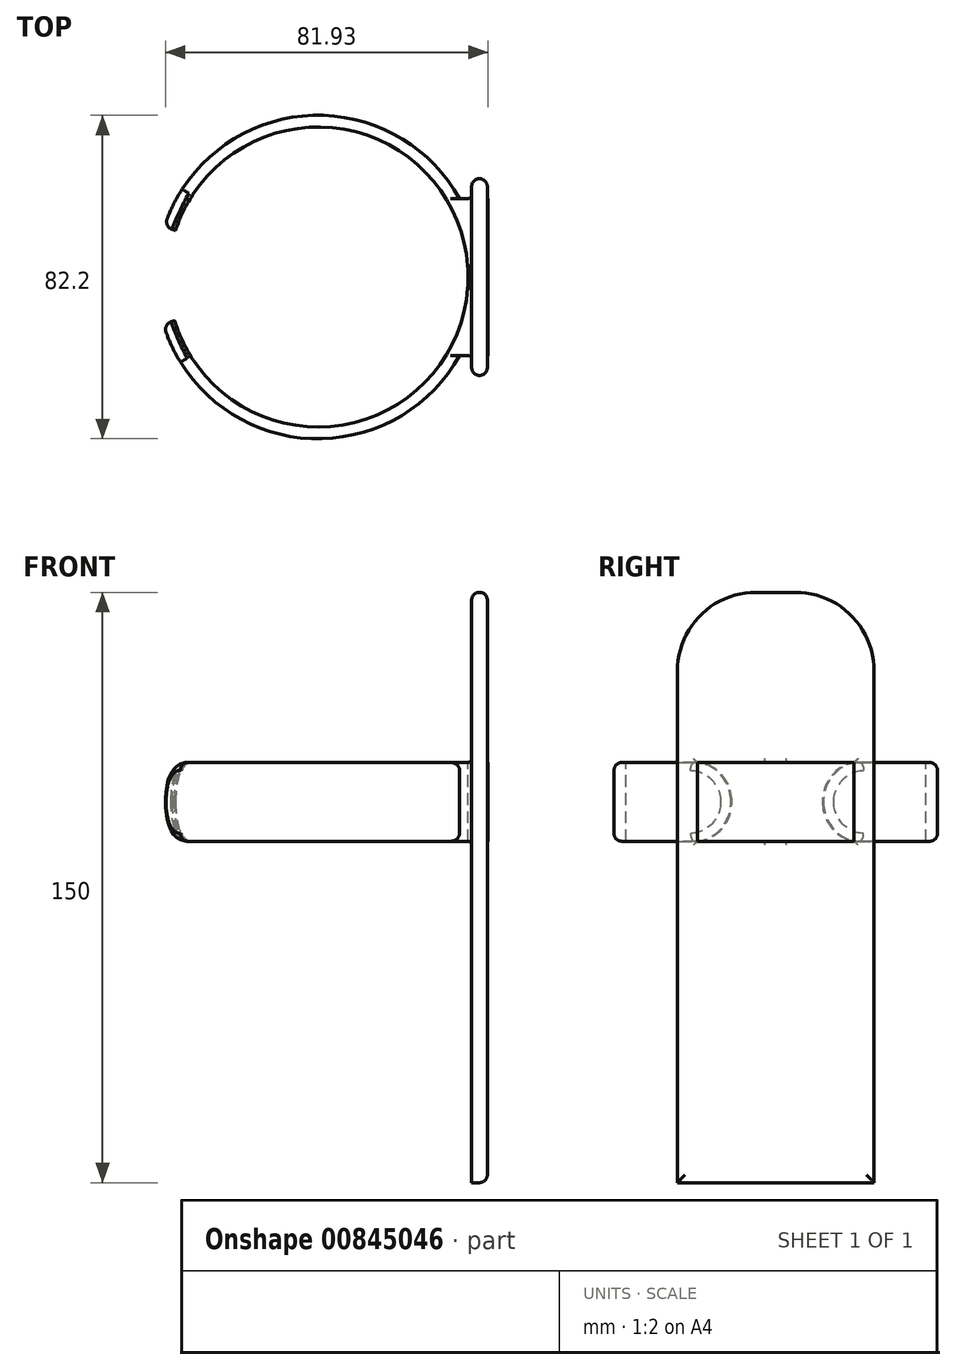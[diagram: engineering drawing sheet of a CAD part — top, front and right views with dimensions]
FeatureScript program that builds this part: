
annotation { "Feature Type Name" : "Feature", "Feature Type Description" : "" }
export const myFeature = defineFeature(function(context is Context, id is Id, definition is map)
    precondition{}
    {
        {
            var Q0;
            Q0=qCreatedBy(makeId("Top.planeOp"),FACE);
            var sketch = newSketch(context, id + "F0", { "sketchPlane" : qUnion([Q0])});
            skArc(sketch, "E0", {"start": v(-39.31, -11.99) * mm, "mid": v(41.1, -0.41) * mm, "end": v(-39.06, 12.77) * mm});
            skArc(sketch, "E1.0", {"start": v(-36.44, -11.11) * mm, "mid": v(38.1, -0.38) * mm, "end": v(-36.21, 11.84) * mm});
            skLineSegment(sketch, "E2", {"start": v(-39.06, 12.77) * mm, "end": v(-36.21, 11.84) * mm});
            skLineSegment(sketch, "E3", {"start": v(-36.44, -11.11) * mm, "end": v(-39.31, -11.99) * mm});
            skLineSegment(sketch, "E4", {"start": v(35.95, 19.92) * mm, "end": v(43.16, 19.92) * mm});
            skLineSegment(sketch, "E5", {"start": v(43.16, 19.92) * mm, "end": v(43.16, 0) * mm});
            skLineSegment(sketch, "E6.MirrorCS", {"start": v(43.16, -19.92) * mm, "end": v(43.16, 0) * mm});
            skLineSegment(sketch, "E7.MirrorCS", {"start": v(35.95, -19.92) * mm, "end": v(43.16, -19.92) * mm});
            skSolve(sketch);
        }
        {
            var Q0;
            Q0=makeQuery(id+"F0.imprint","IMPRINT",FACE,{"disambiguationData":[TD([[makeQuery(id+"F0.imprint","IMPRINT",EDGE,{"derivedFrom":sQuery(id+"F0.wireOp",EDGE,"E0")}),1.0]])]});
            var Q1;
            {var subQ0=sQuery(id+"F0.wireOp",EDGE,"E4");Q1=makeQuery(id+"F0.imprint","IMPRINT",FACE,{"disambiguationData":[TD([[makeQuery(id+"F0.imprint","IMPRINT",EDGE,{"derivedFrom":subQ0}),-1.0]])]});}
            extrude(context, id + "F1", {"entities" : qUnion([Q0, Q1]), "oppositeDirection" : true, "depth" : 20 * mm, "offsetDistance" : 25 * mm});
        }
        {
            var Q0;
            Q0=makeQuery(id+"F1.opExtrude","CAP_EDGE",EDGE,{"disambiguationData":[OSD([sQuery(id+"F0.wireOp",EDGE,"E2")])],"isStart":false});
            var Q1;
            Q1=makeQuery(id+"F1.opExtrude","CAP_EDGE",EDGE,{"disambiguationData":[OSD([sQuery(id+"F0.wireOp",EDGE,"E2")])],"isStart":true});
            var Q2;
            Q2=makeQuery(id+"F1.opExtrude","CAP_EDGE",EDGE,{"disambiguationData":[OSD([sQuery(id+"F0.wireOp",EDGE,"E3")])],"isStart":true});
            var Q3;
            Q3=makeQuery(id+"F1.opExtrude","CAP_EDGE",EDGE,{"disambiguationData":[OSD([sQuery(id+"F0.wireOp",EDGE,"E3")])],"isStart":false});
            fillet(context, id + "F2", {"entities" : qUnion([Q0, Q1, Q2, Q3]), "radius" : 10 * mm, "tangentPropagation" : true, "allowEdgeOverflow" : false});
        }
        {
            var Q0;
            Q0=makeQuery(id+"F1.opExtrude","CAP_EDGE",EDGE,{"disambiguationData":[OSD([sQuery(id+"F0.wireOp",EDGE,"E0")])],"isStart":true});
            fillet(context, id + "F3", {"entities" : qUnion([Q0]), "radius" : 2 * mm, "tangentPropagation" : true, "allowEdgeOverflow" : false});
        }
        {
            var Q0;
            Q0=qCreatedBy(makeId("Right.planeOp"),FACE);
            cPlane(context, id + "F4", {"entities" : qUnion([Q0]), "cplaneType" : CPlaneType.OFFSET, "offset" : 39 * mm, "width" : 150 * mm, "height" : 150 * mm});
        }
        {
            var Q0;
            Q0=qCreatedBy(id+"F4.planeOp",FACE);
            var sketch = newSketch(context, id + "F5", { "sketchPlane" : qUnion([Q0])});
            skLineSegment(sketch, "E8", {"start": v(0, 43.25) * mm, "end": v(25, 43.25) * mm});
            skLineSegment(sketch, "E9", {"start": v(25, 43.25) * mm, "end": v(25, -106.75) * mm});
            skLineSegment(sketch, "E10", {"start": v(25, -106.75) * mm, "end": v(0, -106.75) * mm});
            skLineSegment(sketch, "E11.MirrorCS", {"start": v(-25, -106.75) * mm, "end": v(0, -106.75) * mm});
            skLineSegment(sketch, "E12.MirrorCS", {"start": v(0, 43.25) * mm, "end": v(-25, 43.25) * mm});
            skLineSegment(sketch, "E13.MirrorCS", {"start": v(-25, 43.25) * mm, "end": v(-25, -106.75) * mm});
            skSolve(sketch);
        }
        {
            var Q0;
            Q0=makeQuery(id+"F5.imprint","IMPRINT",FACE,{"disambiguationData":[TD([[makeQuery(id+"F5.imprint","IMPRINT",EDGE,{"derivedFrom":sQuery(id+"F5.wireOp",EDGE,"E8")}),-1.0]])]});
            extrude(context, id + "F6", {"entities" : qUnion([Q0]), "operationType" : NewBodyOperationType.ADD, "depth" : 4 * mm, "offsetDistance" : 25 * mm});
        }
        {
            var Q0;
            Q0=makeQuery(id+"F6.opExtrude","SWEPT_EDGE",EDGE,{"disambiguationData":[OSD([sQuery(id+"F5.wireOp",EDGE,"E12.MirrorCS"),sQuery(id+"F5.wireOp",EDGE,"E13.MirrorCS")])]});
            var Q1;
            Q1=makeQuery(id+"F6.opExtrude","SWEPT_EDGE",EDGE,{"disambiguationData":[OSD([sQuery(id+"F5.wireOp",EDGE,"E8"),sQuery(id+"F5.wireOp",EDGE,"E9")])]});
            fillet(context, id + "F7", {"entities" : qUnion([Q0, Q1]), "radius" : 20 * mm, "tangentPropagation" : true, "allowEdgeOverflow" : false});
        }
        {
            var Q0;
            Q0=makeQuery(id+"F6.opExtrude","CAP_EDGE",EDGE,{"disambiguationData":[OSD([sQuery(id+"F5.wireOp",EDGE,"E13.MirrorCS")])],"isStart":false});
            var Q1;
            Q1=makeQuery(id+"F6.opExtrude","CAP_EDGE",EDGE,{"disambiguationData":[OSD([sQuery(id+"F5.wireOp",EDGE,"E13.MirrorCS")])],"isStart":true});
            var Q2;
            Q2=makeQuery(id+"F6.opExtrude","CAP_EDGE",EDGE,{"disambiguationData":[OSD([sQuery(id+"F5.wireOp",EDGE,"E10"),sQuery(id+"F5.wireOp",EDGE,"E11.MirrorCS")])],"isStart":false});
            fillet(context, id + "F8", {"entities" : qUnion([Q0, Q1, Q2]), "radius" : 2 * mm, "tangentPropagation" : true, "allowEdgeOverflow" : false});
        }
        {
            var Q0;
            Q0=makeQuery(id+"F1.opExtrude","SWEPT_FACE",FACE,{"disambiguationData":[OSD([sQuery(id+"F0.wireOp",EDGE,"E5"),sQuery(id+"F0.wireOp",EDGE,"E6.MirrorCS")])]});
            extrude(context, id + "F9", {"entities" : qUnion([Q0]), "operationType" : NewBodyOperationType.ADD, "oppositeDirection" : true, "depth" : 2 * mm, "offsetDistance" : 25 * mm});
        }
        {
            var Q0;
            Q0=makeQuery(id+"F1.opExtrude","SWEPT_FACE",FACE,{"disambiguationData":[OSD([sQuery(id+"F0.wireOp",EDGE,"E5"),sQuery(id+"F0.wireOp",EDGE,"E6.MirrorCS")])]});
            extrude(context, id + "F10", {"entities" : qUnion([Q0]), "operationType" : NewBodyOperationType.ADD, "oppositeDirection" : true, "depth" : 4 * mm, "offsetDistance" : 25 * mm});
        }
        {
            var Q0;
            Q0=makeQuery(id+"F6.boolean.opBoolean","INTERSECT",EDGE,{"derivedFrom":[makeQuery(id+"F1.opExtrude","CAP_FACE",FACE,{"disambiguationData":[OSD([sQuery(id+"F0.wireOp",EDGE,"E0"),sQuery(id+"F0.wireOp",EDGE,"E1.0"),sQuery(id+"F0.wireOp",EDGE,"E2"),sQuery(id+"F0.wireOp",EDGE,"E3"),sQuery(id+"F0.wireOp",EDGE,"E4"),sQuery(id+"F0.wireOp",EDGE,"E5"),sQuery(id+"F0.wireOp",EDGE,"E6.MirrorCS"),sQuery(id+"F0.wireOp",EDGE,"E7.MirrorCS")])],"isStart":true}),makeQuery(id+"F6.opExtrude","CAP_FACE",FACE,{"disambiguationData":[OSD([sQuery(id+"F5.wireOp",EDGE,"E8"),sQuery(id+"F5.wireOp",EDGE,"E9"),sQuery(id+"F5.wireOp",EDGE,"E10"),sQuery(id+"F5.wireOp",EDGE,"E11.MirrorCS"),sQuery(id+"F5.wireOp",EDGE,"E12.MirrorCS"),sQuery(id+"F5.wireOp",EDGE,"E13.MirrorCS")])],"isStart":true})]});
            var Q1;
            Q1=makeQuery(id+"F6.boolean.opBoolean","INTERSECT",EDGE,{"derivedFrom":[makeQuery(id+"F1.opExtrude","CAP_FACE",FACE,{"disambiguationData":[OSD([sQuery(id+"F0.wireOp",EDGE,"E0"),sQuery(id+"F0.wireOp",EDGE,"E1.0"),sQuery(id+"F0.wireOp",EDGE,"E2"),sQuery(id+"F0.wireOp",EDGE,"E3"),sQuery(id+"F0.wireOp",EDGE,"E4"),sQuery(id+"F0.wireOp",EDGE,"E5"),sQuery(id+"F0.wireOp",EDGE,"E6.MirrorCS"),sQuery(id+"F0.wireOp",EDGE,"E7.MirrorCS")])],"isStart":false}),makeQuery(id+"F6.opExtrude","CAP_FACE",FACE,{"disambiguationData":[OSD([sQuery(id+"F5.wireOp",EDGE,"E8"),sQuery(id+"F5.wireOp",EDGE,"E9"),sQuery(id+"F5.wireOp",EDGE,"E10"),sQuery(id+"F5.wireOp",EDGE,"E11.MirrorCS"),sQuery(id+"F5.wireOp",EDGE,"E12.MirrorCS"),sQuery(id+"F5.wireOp",EDGE,"E13.MirrorCS")])],"isStart":true})]});
            var Q2;
            Q2=makeQuery(id+"F6.boolean.opBoolean","INTERSECT",EDGE,{"derivedFrom":[makeQuery(id+"F1.opExtrude","SWEPT_FACE",FACE,{"disambiguationData":[OSD([sQuery(id+"F0.wireOp",EDGE,"E7.MirrorCS")])]}),makeQuery(id+"F6.opExtrude","CAP_FACE",FACE,{"disambiguationData":[OSD([sQuery(id+"F5.wireOp",EDGE,"E8"),sQuery(id+"F5.wireOp",EDGE,"E9"),sQuery(id+"F5.wireOp",EDGE,"E10"),sQuery(id+"F5.wireOp",EDGE,"E11.MirrorCS"),sQuery(id+"F5.wireOp",EDGE,"E12.MirrorCS"),sQuery(id+"F5.wireOp",EDGE,"E13.MirrorCS")])],"isStart":true})]});
            var Q3;
            Q3=makeQuery(id+"F6.boolean.opBoolean","INTERSECT",EDGE,{"derivedFrom":[makeQuery(id+"F1.opExtrude","SWEPT_FACE",FACE,{"disambiguationData":[OSD([sQuery(id+"F0.wireOp",EDGE,"E4")])]}),makeQuery(id+"F6.opExtrude","CAP_FACE",FACE,{"disambiguationData":[OSD([sQuery(id+"F5.wireOp",EDGE,"E8"),sQuery(id+"F5.wireOp",EDGE,"E9"),sQuery(id+"F5.wireOp",EDGE,"E10"),sQuery(id+"F5.wireOp",EDGE,"E11.MirrorCS"),sQuery(id+"F5.wireOp",EDGE,"E12.MirrorCS"),sQuery(id+"F5.wireOp",EDGE,"E13.MirrorCS")])],"isStart":true})]});
            fillet(context, id + "F11", {"entities" : qUnion([Q0, Q1, Q2, Q3]), "radius" : 1 * mm, "tangentPropagation" : true, "allowEdgeOverflow" : false});
        }
    });
